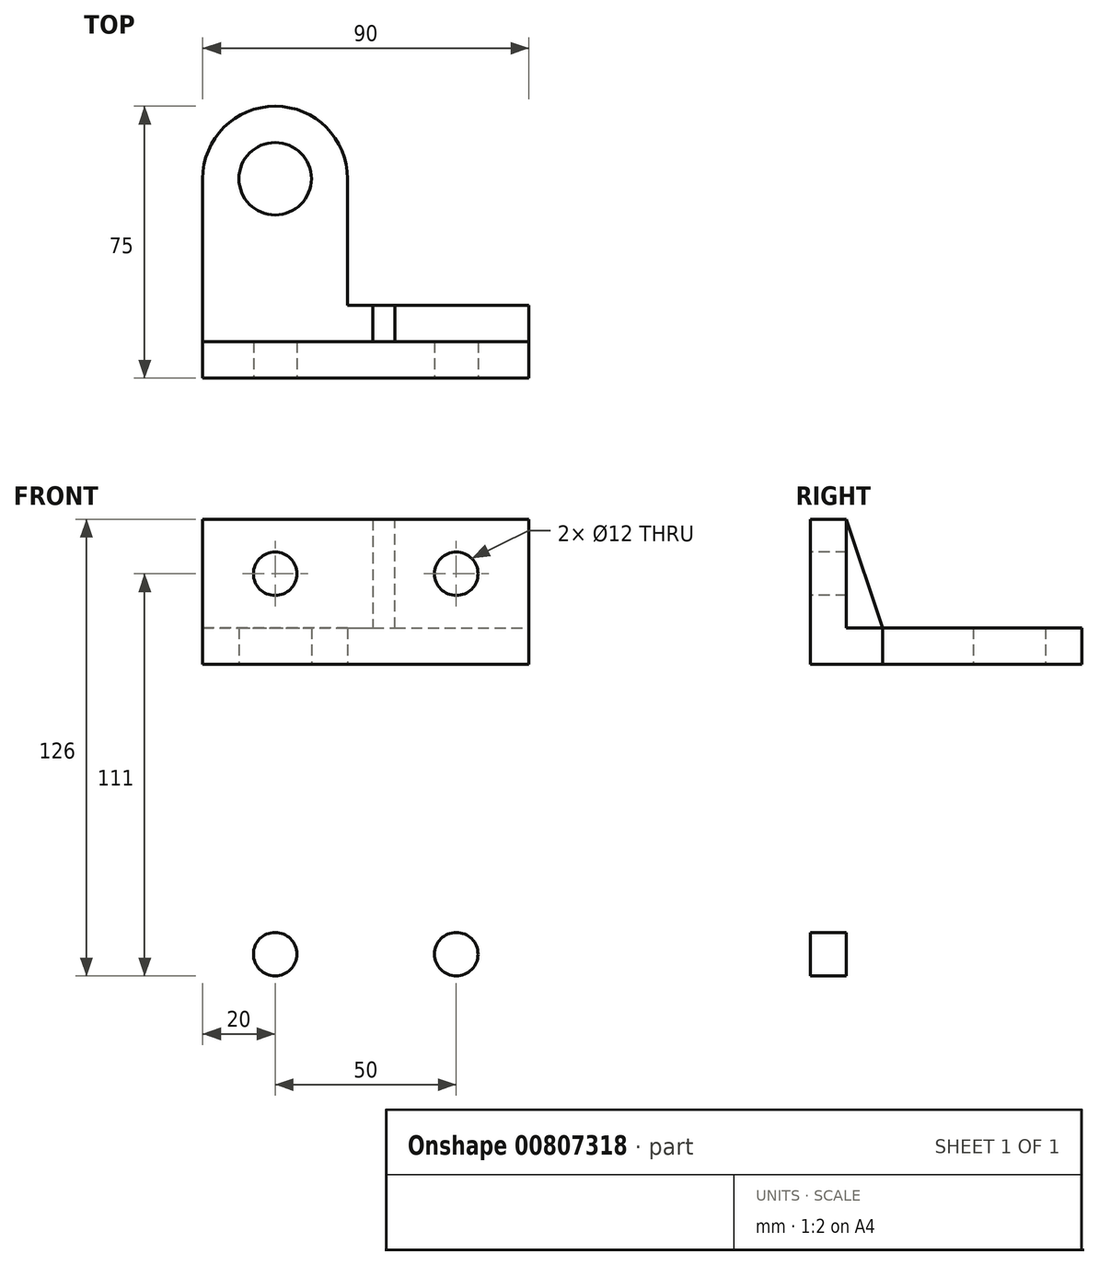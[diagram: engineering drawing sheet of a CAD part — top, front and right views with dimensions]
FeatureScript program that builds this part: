
annotation { "Feature Type Name" : "Feature", "Feature Type Description" : "" }
export const myFeature = defineFeature(function(context is Context, id is Id, definition is map)
    precondition{}
    {
        {
            var Q0;
            Q0=qCreatedBy(makeId("Top.planeOp"),FACE);
            var sketch = newSketch(context, id + "F0", { "sketchPlane" : qUnion([Q0])});
            skLineSegment(sketch, "E0.bottom", {"start": v(0, 0) * mm, "end": v(90, 0) * mm});
            skLineSegment(sketch, "E0.top", {"start": v(0, 10) * mm, "end": v(90, 10) * mm});
            skLineSegment(sketch, "E0.left", {"start": v(0, 0) * mm, "end": v(0, 10) * mm});
            skLineSegment(sketch, "E0.right", {"start": v(90, 0) * mm, "end": v(90, 10) * mm});
            skLineSegment(sketch, "E1", {"start": v(0, 10) * mm, "end": v(0, 55) * mm});
            skLineSegment(sketch, "E2", {"start": v(40, 55) * mm, "end": v(40, 10) * mm});
            skArc(sketch, "E3", {"start": v(0, 55) * mm, "mid": v(20, 35) * mm, "end": v(40, 55) * mm, "construction": true});
            skArc(sketch, "E4", {"start": v(40, 55) * mm, "mid": v(20, 75) * mm, "end": v(0, 55) * mm});
            skCircle(sketch, "E5", {"center": v(20, 55) * mm, "radius": 10 * mm});
            skLineSegment(sketch, "E6", {"start": v(40, 20) * mm, "end": v(90, 20) * mm});
            skLineSegment(sketch, "E7", {"start": v(90, 20) * mm, "end": v(90, 10) * mm});
            skLineSegment(sketch, "E8", {"start": v(90, 20) * mm, "end": v(33.22, 70) * mm});
            skLineSegment(sketch, "E9", {"start": v(53, 10) * mm, "end": v(53, 20) * mm});
            skLineSegment(sketch, "E10", {"start": v(47, 20) * mm, "end": v(47, 10) * mm});
            skSolve(sketch);
        }
        {
            var Q0;
            Q0=makeQuery(id+"F0.imprint","IMPRINT",FACE,{"disambiguationData":[TD([[makeQuery(id+"F0.imprint","IMPRINT",EDGE,{"derivedFrom":sQuery(id+"F0.wireOp",EDGE,"E0.bottom")}),1.0]])]});
            var Q1;
            {var subQ0=sQuery(id+"F0.wireOp",EDGE,"E9");Q1=makeQuery(id+"F0.imprint","IMPRINT",FACE,{"disambiguationData":[TD([[makeQuery(id+"F0.imprint","IMPRINT",EDGE,{"derivedFrom":subQ0}),1.0]])]});}
            extrude(context, id + "F1", {"entities" : qUnion([Q0, Q1]), "endBound" : BoundingType.SYMMETRIC, "oppositeDirection" : true, "depth" : 135 * mm, "offsetDistance" : 25 * mm});
        }
        {
            var Q0;
            {var subQ6=sQuery(id+"F0.wireOp",EDGE,"E1");Q0=makeQuery(id+"F0.imprint","IMPRINT",FACE,{"disambiguationData":[TD([[makeQuery(id+"F0.imprint","IMPRINT",EDGE,{"derivedFrom":subQ6}),-1.0]])]});}
            var Q1;
            {var subQ3=sQuery(id+"F0.wireOp",EDGE,"E10");Q1=makeQuery(id+"F0.imprint","IMPRINT",FACE,{"disambiguationData":[TD([[makeQuery(id+"F0.imprint","IMPRINT",EDGE,{"derivedFrom":subQ3}),-1.0]])]});}
            var Q2;
            {var subQ0=sQuery(id+"F0.wireOp",EDGE,"E7");Q2=makeQuery(id+"F0.imprint","IMPRINT",FACE,{"disambiguationData":[TD([[makeQuery(id+"F0.imprint","IMPRINT",EDGE,{"derivedFrom":subQ0}),-1.0]])]});}
            var Q3;
            {var subQ0=sQuery(id+"F0.wireOp",EDGE,"E9");Q3=makeQuery(id+"F0.imprint","IMPRINT",FACE,{"disambiguationData":[TD([[makeQuery(id+"F0.imprint","IMPRINT",EDGE,{"derivedFrom":subQ0}),1.0]])]});}
            extrude(context, id + "F2", {"entities" : qUnion([Q0, Q1, Q2, Q3]), "operationType" : NewBodyOperationType.ADD, "endBound" : BoundingType.SYMMETRIC, "depth" : 75 * mm, "offsetDistance" : 25 * mm});
        }
        {
            var Q0;
            {var subQ6=sQuery(id+"F0.wireOp",EDGE,"E8");Q0=makeQuery(id+"F0.imprint","IMPRINT",FACE,{"disambiguationData":[TD([[makeQuery(id+"F0.imprint","IMPRINT",EDGE,{"derivedFrom":subQ6}),1.0]])]});}
            extrude(context, id + "F3", {"entities" : qUnion([Q0]), "operationType" : NewBodyOperationType.ADD, "endBound" : BoundingType.SYMMETRIC, "depth" : 6 * mm, "offsetDistance" : 25 * mm});
        }
        {
            var Q0;
            Q0=makeQuery(id+"F2.boolean.opBoolean","MERGE",FACE,{"derivedFrom":[makeQuery(id+"F1.opExtrude","SWEPT_FACE",FACE,{"disambiguationData":[OSD([sQuery(id+"F0.wireOp",EDGE,"E0.right")])]}),makeQuery(id+"F2.opExtrude","SWEPT_FACE",FACE,{"disambiguationData":[OSD([sQuery(id+"F0.wireOp",EDGE,"E7")])]})]});
            var sketch = newSketch(context, id + "F4", { "sketchPlane" : qUnion([Q0])});
            skLineSegment(sketch, "E11.0", {"start": v(20, 37.5) * mm, "end": v(20, 3) * mm});
            skLineSegment(sketch, "E12.0", {"start": v(10, 37.5) * mm, "end": v(10, 67.5) * mm});
            skLineSegment(sketch, "E13.0", {"start": v(20, 37.5) * mm, "end": v(10, 37.5) * mm});
            skLineSegment(sketch, "E14.0", {"start": v(20, -37.5) * mm, "end": v(10, -37.5) * mm});
            skLineSegment(sketch, "E15.0", {"start": v(20, -3) * mm, "end": v(20, -37.5) * mm});
            skLineSegment(sketch, "E16.0", {"start": v(10, -67.5) * mm, "end": v(10, -37.5) * mm});
            skLineSegment(sketch, "E17", {"start": v(20, 37.5) * mm, "end": v(10, 67.5) * mm});
            skLineSegment(sketch, "E18", {"start": v(20, -37.5) * mm, "end": v(10, -67.5) * mm});
            skLineSegment(sketch, "E19", {"start": v(10, 67.5) * mm, "end": v(20, 67.5) * mm});
            skLineSegment(sketch, "E20", {"start": v(20, 67.5) * mm, "end": v(20, 37.5) * mm});
            skLineSegment(sketch, "E21", {"start": v(20, -37.5) * mm, "end": v(20, -67.5) * mm});
            skLineSegment(sketch, "E22", {"start": v(20, -67.5) * mm, "end": v(10, -67.5) * mm});
            skLineSegment(sketch, "E23.0", {"start": v(0, 67.5) * mm, "end": v(10, 67.5) * mm});
            skLineSegment(sketch, "E24.0", {"start": v(0, -67.5) * mm, "end": v(10, -67.5) * mm});
            skLineSegment(sketch, "E25", {"start": v(0, 67.5) * mm, "end": v(0, -67.5) * mm});
            skLineSegment(sketch, "E26", {"start": v(0, 27.5) * mm, "end": v(10, 27.5) * mm});
            skLineSegment(sketch, "E27", {"start": v(10, 27.5) * mm, "end": v(10, -27.5) * mm});
            skLineSegment(sketch, "E28", {"start": v(10, -27.5) * mm, "end": v(0, -27.5) * mm});
            skPoint(sketch, "E29", {"position": v(10, 0) * mm});
            skPoint(sketch, "E30", {"position": v(0, 0) * mm});
            skLineSegment(sketch, "E31", {"start": v(0, 0) * mm, "end": v(31.8, 0) * mm, "construction": true});
            skSolve(sketch);
        }
        {
            var Q0;
            Q0=makeQuery(id+"F4.imprint","IMPRINT",FACE,{"disambiguationData":[TD([[makeQuery(id+"F4.imprint","IMPRINT",EDGE,{"derivedFrom":sQuery(id+"F4.wireOp",EDGE,"E17")}),-1.0]])]});
            var Q1;
            Q1=makeQuery(id+"F4.imprint","IMPRINT",FACE,{"disambiguationData":[TD([[makeQuery(id+"F4.imprint","IMPRINT",EDGE,{"derivedFrom":sQuery(id+"F4.wireOp",EDGE,"E18")}),1.0]])]});
            var Q2;
            {var subQ0=sQuery(id+"F4.wireOp",EDGE,"E26");Q2=makeQuery(id+"F4.imprint","IMPRINT",FACE,{"disambiguationData":[TD([[makeQuery(id+"F4.imprint","IMPRINT",EDGE,{"derivedFrom":subQ0}),-1.0]])]});}
            extrude(context, id + "F5", {"entities" : qUnion([Q0, Q1, Q2]), "operationType" : NewBodyOperationType.REMOVE, "endBound" : BoundingType.THROUGH_ALL, "oppositeDirection" : true, "depth" : 25 * mm, "offsetDistance" : 25 * mm});
        }
        {
            var Q0;
            {var subQ2=sQuery(id+"F0.wireOp",EDGE,"E0.bottom");Q0=makeQuery(id+"F5.boolean.opBoolean","SPLIT",FACE,{"disambiguationData":[TD([makeQuery(id+"F5.opExtrude","SWEPT_FACE",FACE,{"disambiguationData":[OSD([sQuery(id+"F4.wireOp",EDGE,"E26")])]})])],"derivedFrom":makeQuery(id+"F1.opExtrude","SWEPT_FACE",FACE,{"disambiguationData":[OSD([subQ2])]})});}
            var sketch = newSketch(context, id + "F6", { "sketchPlane" : qUnion([Q0])});
            skLineSegment(sketch, "E32.0", {"start": v(0, 67.5) * mm, "end": v(90, 67.5) * mm});
            skLineSegment(sketch, "E33.0", {"start": v(0, -67.5) * mm, "end": v(90, -67.5) * mm});
            skLineSegment(sketch, "E34.0", {"start": v(90, -67.5) * mm, "end": v(90, -27.5) * mm});
            skLineSegment(sketch, "E35.0", {"start": v(0, -67.5) * mm, "end": v(0, -27.5) * mm});
            skLineSegment(sketch, "E36.0", {"start": v(0, 27.5) * mm, "end": v(0, -27.5) * mm});
            skLineSegment(sketch, "E37.0", {"start": v(90, 27.5) * mm, "end": v(90, -27.5) * mm});
            skLineSegment(sketch, "E38.0", {"start": v(90, 27.5) * mm, "end": v(90, 67.5) * mm});
            skLineSegment(sketch, "E39.0", {"start": v(0, 27.5) * mm, "end": v(0, 67.5) * mm});
            skCircle(sketch, "E40", {"center": v(70, 52.5) * mm, "radius": 6 * mm});
            skLineSegment(sketch, "E41", {"start": v(90, 0) * mm, "end": v(0, 0) * mm, "construction": true});
            skCircle(sketch, "E42", {"center": v(20, 52.5) * mm, "radius": 6 * mm});
            skLineSegment(sketch, "E43", {"start": v(90, 52.5) * mm, "end": v(0, 52.5) * mm, "construction": true});
            skCircle(sketch, "E44.MirrorC", {"center": v(70, -52.5) * mm, "radius": 6 * mm});
            skCircle(sketch, "E45.MirrorC", {"center": v(20, -52.5) * mm, "radius": 6 * mm});
            skSolve(sketch);
        }
        {
            var Q0;
            Q0=makeQuery(id+"F6.imprint","IMPRINT",FACE,{"disambiguationData":[TD([[makeQuery(id+"F6.imprint","IMPRINT",EDGE,{"derivedFrom":sQuery(id+"F6.wireOp",EDGE,"E40")}),1.0]])]});
            var Q1;
            Q1=makeQuery(id+"F6.imprint","IMPRINT",FACE,{"disambiguationData":[TD([[makeQuery(id+"F6.imprint","IMPRINT",EDGE,{"derivedFrom":sQuery(id+"F6.wireOp",EDGE,"E42")}),1.0]])]});
            var Q2;
            Q2=makeQuery(id+"F6.imprint","IMPRINT",FACE,{"disambiguationData":[TD([[makeQuery(id+"F6.imprint","IMPRINT",EDGE,{"derivedFrom":sQuery(id+"F6.wireOp",EDGE,"E44.MirrorC")}),-1.0]])]});
            var Q3;
            Q3=makeQuery(id+"F6.imprint","IMPRINT",FACE,{"disambiguationData":[TD([[makeQuery(id+"F6.imprint","IMPRINT",EDGE,{"derivedFrom":sQuery(id+"F6.wireOp",EDGE,"E45.MirrorC")}),-1.0]])]});
            extrude(context, id + "F7", {"entities" : qUnion([Q0, Q1, Q2, Q3]), "operationType" : NewBodyOperationType.REMOVE, "endBound" : BoundingType.THROUGH_ALL, "oppositeDirection" : true, "depth" : 25 * mm, "offsetDistance" : 25 * mm});
        }
    });
